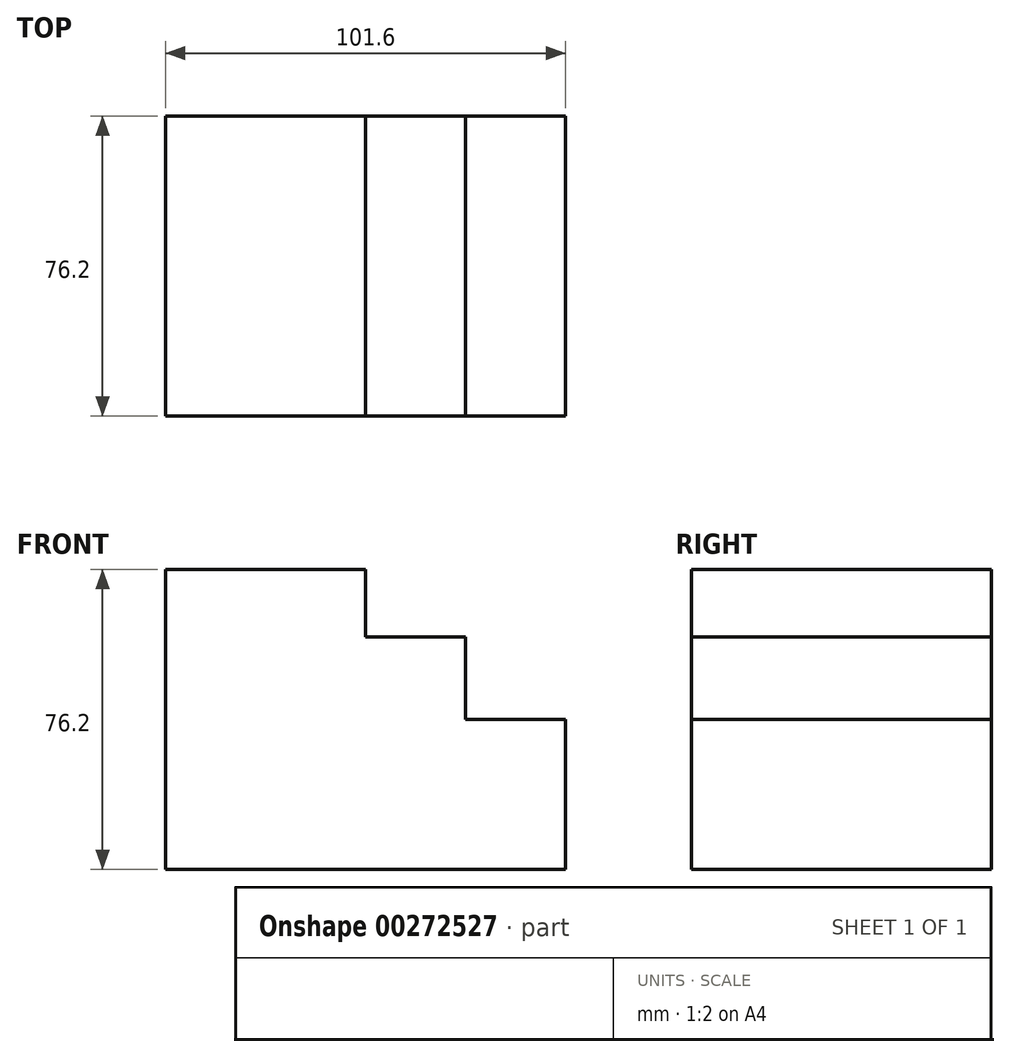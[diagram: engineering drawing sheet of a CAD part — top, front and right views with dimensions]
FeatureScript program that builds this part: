
annotation { "Feature Type Name" : "Feature", "Feature Type Description" : "" }
export const myFeature = defineFeature(function(context is Context, id is Id, definition is map)
    precondition{}
    {
        {
            var Q0;
            Q0=qCreatedBy(makeId("Front.planeOp"),FACE);
            var sketch = newSketch(context, id + "F0", { "sketchPlane" : qUnion([Q0])});
            skLineSegment(sketch, "E0.bottom", {"start": v(0, 0) * mm, "end": v(-50.8, 0) * mm});
            skLineSegment(sketch, "E0.top", {"start": v(0, 76.2) * mm, "end": v(-50.8, 76.2) * mm});
            skLineSegment(sketch, "E0.left", {"start": v(0, 0) * mm, "end": v(0, 76.2) * mm});
            skLineSegment(sketch, "E0.right", {"start": v(-50.8, 0) * mm, "end": v(-50.8, 76.2) * mm});
            skSolve(sketch);
        }
        {
            var Q0;
            Q0 = qSketchRegion(id + "F0", true);
            extrude(context, id + "F1", {"entities" : qUnion([Q0]), "depth" : 76.2 * mm});
        }
        {
            var Q0;
            Q0=makeQuery(id+"F1.opExtrude","SWEPT_FACE",FACE,{"disambiguationData":[OSD([sQuery(id+"F0.wireOp",EDGE,"E0.left")])]});
            var sketch = newSketch(context, id + "F2", { "sketchPlane" : qUnion([Q0])});
            skLineSegment(sketch, "E1.bottom", {"start": v(0, 0) * mm, "end": v(-76.2, 0) * mm});
            skLineSegment(sketch, "E1.top", {"start": v(0, 38.1) * mm, "end": v(-76.2, 38.1) * mm});
            skLineSegment(sketch, "E1.left", {"start": v(0, 0) * mm, "end": v(0, 38.1) * mm});
            skLineSegment(sketch, "E1.right", {"start": v(-76.2, 0) * mm, "end": v(-76.2, 38.1) * mm});
            skSolve(sketch);
        }
        {
            var Q0;
            Q0=makeQuery(id+"F2.imprint","IMPRINT",FACE,{"disambiguationData":[TD([[makeQuery(id+"F2.imprint","IMPRINT",EDGE,{"derivedFrom":sQuery(id+"F2.wireOp",EDGE,"E1.bottom")}),1.0]])]});
            extrude(context, id + "F3", {"entities" : qUnion([Q0]), "operationType" : NewBodyOperationType.ADD, "depth" : 50.8 * mm});
        }
        {
            var Q0;
            Q0=makeQuery(id+"F1.opExtrude","SWEPT_FACE",FACE,{"disambiguationData":[OSD([sQuery(id+"F0.wireOp",EDGE,"E0.left")])]});
            var sketch = newSketch(context, id + "F4", { "sketchPlane" : qUnion([Q0])});
            skLineSegment(sketch, "E2.bottom", {"start": v(0, 38.1) * mm, "end": v(-76.2, 38.1) * mm});
            skLineSegment(sketch, "E2.top", {"start": v(0, 59) * mm, "end": v(-76.2, 59) * mm});
            skLineSegment(sketch, "E2.left", {"start": v(0, 38.1) * mm, "end": v(0, 59) * mm});
            skLineSegment(sketch, "E2.right", {"start": v(-76.2, 38.1) * mm, "end": v(-76.2, 59) * mm});
            skSolve(sketch);
        }
        {
            var Q0;
            Q0=makeQuery(id+"F4.imprint","IMPRINT",FACE,{"disambiguationData":[TD([[makeQuery(id+"F4.imprint","IMPRINT",EDGE,{"derivedFrom":sQuery(id+"F4.wireOp",EDGE,"E2.bottom")}),-1.0]])]});
            extrude(context, id + "F5", {"entities" : qUnion([Q0]), "operationType" : NewBodyOperationType.ADD, "depth" : 25.4 * mm});
        }
    });
